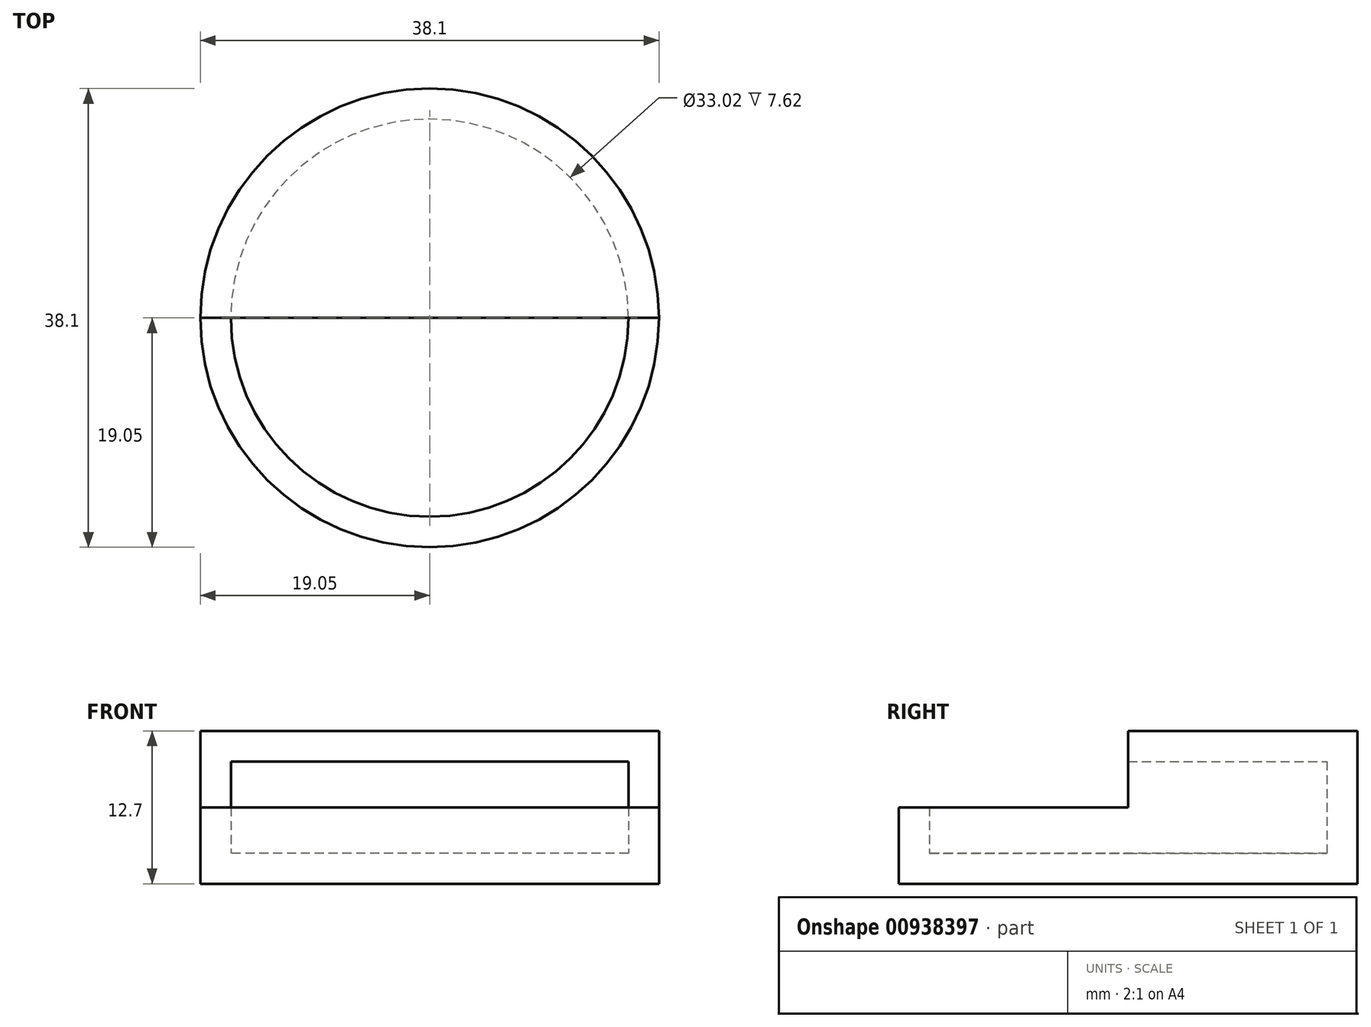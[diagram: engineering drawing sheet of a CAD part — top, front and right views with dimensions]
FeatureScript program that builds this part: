
annotation { "Feature Type Name" : "Feature", "Feature Type Description" : "" }
export const myFeature = defineFeature(function(context is Context, id is Id, definition is map)
    precondition{}
    {
        {
            var Q0;
            Q0=qCreatedBy(makeId("Top.planeOp"),FACE);
            var sketch = newSketch(context, id + "F0", { "sketchPlane" : qUnion([Q0])});
            skCircle(sketch, "E0", {"center": v(0, 0) * mm, "radius": 19.05 * mm});
            skSolve(sketch);
        }
        {
            var Q0;
            Q0=makeQuery(id+"F0.imprint","IMPRINT",FACE,{"disambiguationData":[TD([[makeQuery(id+"F0.imprint","IMPRINT",EDGE,{"derivedFrom":sQuery(id+"F0.wireOp",EDGE,"E0")}),1.0]])]});
            extrude(context, id + "F1", {"entities" : qUnion([Q0]), "depth" : 12.7 * mm, "offsetDistance" : 25.4 * mm});
        }
        {
            var Q0;
            Q0=makeQuery(id+"F1.opExtrude","CAP_FACE",FACE,{"disambiguationData":[OSD([sQuery(id+"F0.wireOp",EDGE,"E0")])],"isStart":false});
            var sketch = newSketch(context, id + "F2", { "sketchPlane" : qUnion([Q0])});
            skLineSegment(sketch, "E1.bottom", {"start": v(-19.05, 0) * mm, "end": v(19.24, 0) * mm});
            skLineSegment(sketch, "E1.top", {"start": v(-19.05, -19.43) * mm, "end": v(19.24, -19.43) * mm});
            skLineSegment(sketch, "E1.left", {"start": v(-19.05, 0) * mm, "end": v(-19.05, -19.43) * mm});
            skLineSegment(sketch, "E1.right", {"start": v(19.24, 0) * mm, "end": v(19.24, -19.43) * mm});
            skSolve(sketch);
        }
        {
            var Q0;
            Q0=makeQuery(id+"F2.imprint","IMPRINT",FACE,{"disambiguationData":[TD([[makeQuery(id+"F2.imprint","IMPRINT",EDGE,{"derivedFrom":sQuery(id+"F2.wireOp",EDGE,"E1.top")}),1.0]])]});
            var Q1;
            {var subQ0=sQuery(id+"F2.wireOp",EDGE,"E1.bottom");var subQ1=makeQuery(id+"F1.opExtrude","CAP_EDGE",EDGE,{"disambiguationData":[OSD([sQuery(id+"F0.wireOp",EDGE,"E0")])],"isStart":false});var subQ3=makeQuery(id+"F2.imprint","INTERSECT",VERTEX,{"derivedFrom":[subQ1,subQ0]});Q1=makeQuery(id+"F2.imprint","IMPRINT",FACE,{"disambiguationData":[TD([[makeQuery(id+"F2.imprint","IMPRINT",EDGE,{"disambiguationData":[TD([[subQ3,1.0]])],"derivedFrom":subQ0}),-1.0]])]});}
            extrude(context, id + "F3", {"entities" : qUnion([Q0, Q1]), "operationType" : NewBodyOperationType.REMOVE, "oppositeDirection" : true, "depth" : 6.35 * mm, "offsetDistance" : 25.4 * mm});
        }
        {
            var Q0;
            Q0=makeQuery(id+"F3.boolean.opBoolean","COPY",FACE,{"derivedFrom":makeQuery(id+"F3.opExtrude","SWEPT_FACE",FACE,{"disambiguationData":[OSD([sQuery(id+"F2.wireOp",EDGE,"E1.bottom")])]})});
            var Q1;
            Q1=makeQuery(id+"F3.boolean.opBoolean","COPY",FACE,{"derivedFrom":makeQuery(id+"F3.opExtrude","CAP_FACE",FACE,{"disambiguationData":[OSD([sQuery(id+"F2.wireOp",EDGE,"E1.bottom"),sQuery(id+"F2.wireOp",EDGE,"E1.top"),sQuery(id+"F2.wireOp",EDGE,"E1.left"),sQuery(id+"F2.wireOp",EDGE,"E1.right")])],"isStart":false})});
            shell(context, id + "F4", {"entities" : qUnion([Q0, Q1]), "thickness" : 2.54 * mm});
        }
        {
            var Q0;
            Q0=makeQuery(id+"F1.opExtrude","CAP_FACE",FACE,{"disambiguationData":[OSD([sQuery(id+"F0.wireOp",EDGE,"E0")])],"isStart":false});
            var sketch = newSketch(context, id + "F5", { "sketchPlane" : qUnion([Q0])});
            skCircle(sketch, "E2", {"center": v(0, 0) * mm, "radius": 6.99 * mm});
            skSolve(sketch);
        }
        {
            var Q0;
            {var subQ0=sQuery(id+"F5.wireOp",EDGE,"E2");var subQ1=makeQuery(id+"F3.boolean.opBoolean","COPY",EDGE,{"derivedFrom":makeQuery(id+"F3.opExtrude","CAP_EDGE",EDGE,{"disambiguationData":[OSD([sQuery(id+"F2.wireOp",EDGE,"E1.bottom")])],"isStart":true})});var subQ2=makeQuery(id+"F5.imprint","INTERSECT",VERTEX,{"disambiguationData":[OD(0.0)],"derivedFrom":[subQ1,subQ0]});Q0=makeQuery(id+"F5.imprint","IMPRINT",FACE,{"disambiguationData":[TD([[makeQuery(id+"F5.imprint","IMPRINT",EDGE,{"disambiguationData":[TD([[subQ2,1.0]])],"derivedFrom":subQ0}),1.0]])]});}
            extrude(context, id + "F6", {"entities" : qUnion([Q0]), "operationType" : NewBodyOperationType.REMOVE, "oppositeDirection" : true, "depth" : 5.08 * mm, "offsetDistance" : 25.4 * mm});
        }
    });
